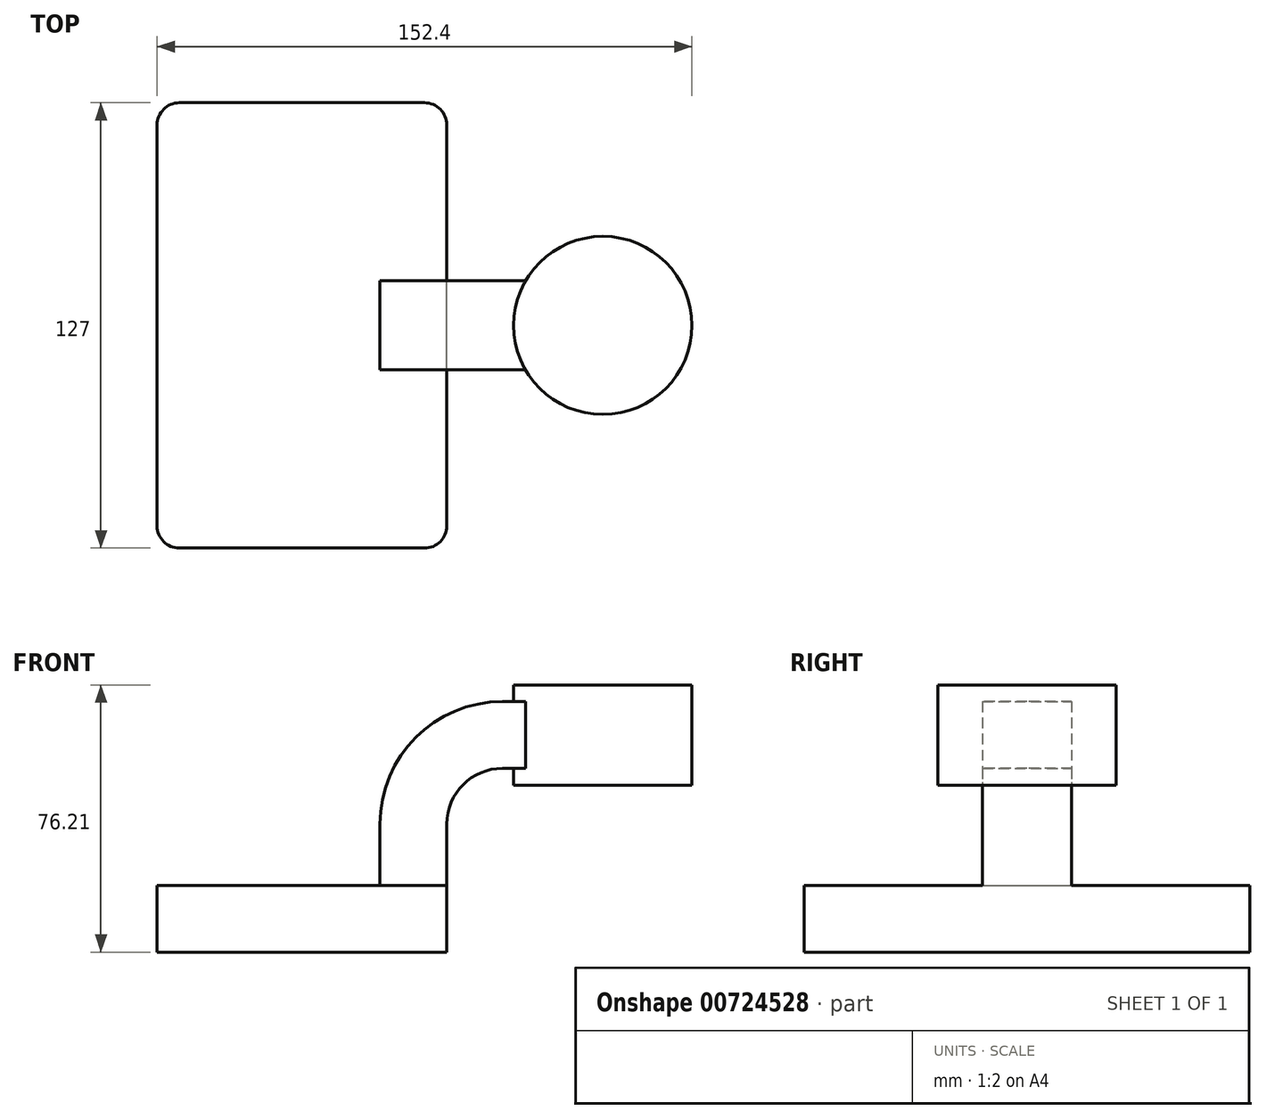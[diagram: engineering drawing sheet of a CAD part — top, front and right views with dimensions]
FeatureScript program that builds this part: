
annotation { "Feature Type Name" : "Feature", "Feature Type Description" : "" }
export const myFeature = defineFeature(function(context is Context, id is Id, definition is map)
    precondition{}
    {
        {
            var Q0;
            Q0=qCreatedBy(makeId("Front.planeOp"),FACE);
            var sketch = newSketch(context, id + "F0", { "sketchPlane" : qUnion([Q0])});
            skLineSegment(sketch, "E0.bottom", {"start": v(41.28, 9.53) * mm, "end": v(-41.28, 9.53) * mm});
            skLineSegment(sketch, "E0.top", {"start": v(41.28, -9.53) * mm, "end": v(-41.28, -9.53) * mm});
            skLineSegment(sketch, "E0.left", {"start": v(41.28, 9.53) * mm, "end": v(41.28, -9.53) * mm});
            skLineSegment(sketch, "E0.right", {"start": v(-41.28, 9.53) * mm, "end": v(-41.28, -9.53) * mm});
            skPoint(sketch, "E0.middle", {"position": v(0, 0) * mm});
            skLineSegment(sketch, "E1.bottom", {"start": v(60.32, 38.1) * mm, "end": v(111.13, 38.1) * mm});
            skLineSegment(sketch, "E1.top", {"start": v(60.32, 66.67) * mm, "end": v(111.13, 66.67) * mm});
            skLineSegment(sketch, "E1.left", {"start": v(60.33, 38.1) * mm, "end": v(60.33, 66.67) * mm});
            skLineSegment(sketch, "E1.right", {"start": v(111.13, 38.1) * mm, "end": v(111.13, 66.67) * mm});
            skPoint(sketch, "E1.middle", {"position": v(85.73, 52.39) * mm});
            skLineSegment(sketch, "E2", {"start": v(41.28, 9.53) * mm, "end": v(41.28, 27) * mm});
            skArc(sketch, "E3", {"start": v(41.27, 27) * mm, "mid": v(45.92, 38.23) * mm, "end": v(57.15, 42.88) * mm});
            skLineSegment(sketch, "E4", {"start": v(57.15, 42.88) * mm, "end": v(85.73, 42.88) * mm});
            skPoint(sketch, "E5", {"position": v(85.73, 38.1) * mm});
            skLineSegment(sketch, "E6.0", {"start": v(57.15, 61.93) * mm, "end": v(85.8, 61.93) * mm});
            skArc(sketch, "E6.1", {"start": v(22.22, 27) * mm, "mid": v(32.45, 51.7) * mm, "end": v(57.15, 61.93) * mm});
            skLineSegment(sketch, "E6.2", {"start": v(22.23, 9.52) * mm, "end": v(22.23, 27) * mm});
            skFitSpline(sketch, "E7", {"points": [v(-41.28, 9.53) * mm, v(57.15, 61.93) * mm], "startDerivative": vector(0.36, 82.92) * mm, "endDerivative": vector(138.46, 0) * mm});
            skLineSegment(sketch, "E8", {"start": v(85.73, 38.1) * mm, "end": v(85.73, 66.67) * mm});
            skLineSegment(sketch, "E9", {"start": v(85.8, 61.93) * mm, "end": v(-14.16, 61.93) * mm, "construction": true});
            skSolve(sketch);
        }
        {
            var Q0;
            Q0=makeQuery(id+"F0.imprint","IMPRINT",FACE,{"disambiguationData":[TD([[makeQuery(id+"F0.imprint","IMPRINT",EDGE,{"derivedFrom":sQuery(id+"F0.wireOp",EDGE,"E0.bottom")}),1.0]])]});
            extrude(context, id + "F1", {"entities" : qUnion([Q0]), "endBound" : BoundingType.SYMMETRIC, "depth" : 127 * mm});
        }
        {
            var Q0;
            {var subQ0=sQuery(id+"F0.wireOp",EDGE,"E4");var subQ1=sQuery(id+"F0.wireOp",EDGE,"E1.left");var subQ2=makeQuery(id+"F0.imprint","INTERSECT",VERTEX,{"derivedFrom":[subQ1,subQ0]});Q0=makeQuery(id+"F0.imprint","IMPRINT",FACE,{"disambiguationData":[TD([[makeQuery(id+"F0.imprint","IMPRINT",EDGE,{"disambiguationData":[TD([[subQ2,-1.0]])],"derivedFrom":subQ1}),-1.0]])]});}
            var Q1;
            {var subQ1=sQuery(id+"F0.wireOp",EDGE,"E2");Q1=makeQuery(id+"F0.imprint","IMPRINT",FACE,{"disambiguationData":[TD([[makeQuery(id+"F0.imprint","IMPRINT",EDGE,{"derivedFrom":subQ1}),1.0]])]});}
            extrude(context, id + "F2", {"entities" : qUnion([Q0, Q1]), "endBound" : BoundingType.SYMMETRIC, "depth" : 25.4 * mm});
        }
        {
            var Q0;
            Q0=makeQuery(id+"F0.imprint","IMPRINT",FACE,{"disambiguationData":[TD([[makeQuery(id+"F0.imprint","IMPRINT",EDGE,{"derivedFrom":sQuery(id+"F0.wireOp",EDGE,"E6.1")}),1.0]])]});
            extrude(context, id + "F3", {"entities" : qUnion([Q0]), "operationType" : NewBodyOperationType.ADD, "endBound" : BoundingType.SYMMETRIC, "depth" : 15.88 * mm});
        }
        {
            var Q0;
            {var subQ4=sQuery(id+"F0.wireOp",EDGE,"E1.right");Q0=makeQuery(id+"F0.imprint","IMPRINT",FACE,{"disambiguationData":[TD([[makeQuery(id+"F0.imprint","IMPRINT",EDGE,{"derivedFrom":subQ4}),1.0]])]});}
            var Q1;
            Q1=sQuery(id+"F0.wireOp",EDGE,"E8");
            revolve(context, id + "F4", {"operationType" : NewBodyOperationType.ADD, "entities" : qUnion([Q0]), "axis" : qUnion([Q1]), "revolveType" : RevolveType.FULL});
        }
        {
            var Q0;
            Q0=makeQuery(id+"F1.opExtrude","CAP_EDGE",EDGE,{"disambiguationData":[OSD([sQuery(id+"F0.wireOp",EDGE,"E0.right")])],"isStart":false});
            var Q1;
            Q1=makeQuery(id+"F1.opExtrude","CAP_EDGE",EDGE,{"disambiguationData":[OSD([sQuery(id+"F0.wireOp",EDGE,"E0.left")])],"isStart":false});
            var Q2;
            Q2=makeQuery(id+"F1.opExtrude","CAP_EDGE",EDGE,{"disambiguationData":[OSD([sQuery(id+"F0.wireOp",EDGE,"E0.left")])],"isStart":true});
            var Q3;
            Q3=makeQuery(id+"F1.opExtrude","CAP_EDGE",EDGE,{"disambiguationData":[OSD([sQuery(id+"F0.wireOp",EDGE,"E0.right")])],"isStart":true});
            fillet(context, id + "F5", {"entities" : qUnion([Q0, Q1, Q2, Q3]), "radius" : 6.35 * mm, "tangentPropagation" : true, "allowEdgeOverflow" : false});
        }
    });
